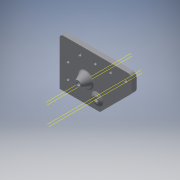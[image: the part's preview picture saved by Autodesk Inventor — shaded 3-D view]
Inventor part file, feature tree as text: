
AUTODESK INVENTOR PART (.ipt)
format: ipt  version: 2018 (Build 220112000, 112)  size: 218,112 bytes
history: native  units: in
note: dims shown in document units (in); Inventor stores cm internally (conversion verified against a paired STEP export)
features: sketch x8, extrude x6, plane x4, revolve x2, fillet x2, projected_geometry x2
ambient origin geometry x8: Origin, YZ Plane, XZ Plane, XY Plane, X Axis, Y Axis, Z Axis, Center Point
bodies: Solid1 (feature_tree)
feature tree (24):
  extrude  "Extrusion1"  Depth=0.7874in
  extrude  "Extrusion2"  Depth=3.5433in
  plane  "Work Plane2"
  revolve  "Revolution1"  [1 undecoded]
  extrude  "Extrusion3"  Depth=0.5512in
  extrude  "Extrusion4"  [1 undecoded]
  fillet  "Fillet1"  Radius=0.3543in
  extrude  "Extrusion5"  TaperAngle=90.0deg  [1 undecoded]
  plane  "Work Plane4"
  revolve  "Revolution2"  [1 undecoded]
  fillet  "Fillet2"  Radius=0.1654in
  extrude  "Extrusion6"  Depth=0.3937in
  sketch  "Sketch1"  dims[d0=0.7874in d1=0.7874in]
  sketch  "Sketch2"  dims[d2=3.5433in d3=3.5433in]
  plane  "Work Plane1"
  sketch  "Sketch3"  dims[d4=0.2362in d5=0.0in d6=0.1969in]
  sketch  "Sketch4"  dims[d7=1.2992in d8=0.5512in]
  projected_geometry  "Projected Loop1"
  sketch  "Sketch5"  dims[d9=0.2362in d10=0.0in d11=-0.0984in d12=0.3543in]
  sketch  "Sketch7"  dims[d13=0.3937in d14=90.0deg]
  plane  "Work Plane3"
  sketch  "Sketch8"  dims[d15=0.2362in d16=0.0in d17=0.1575in d18=0.1654in]
  projected_geometry  "Projected Loop2"
  sketch  "Sketch9"  dims[d19=0.315in d20=0.748in d21=0.748in d22=0.748in d23=0.315in d24=0.748in d25=0.748in d26=0.748in d27=0.2362in d28=0.0in d29=0.0787in d30=0.3543in d32=0.3543in d33=0.1969in d34=0.0in d35=0.0984in d36=0.1969in d37=0.0591in d38=0.0787in d39=90.0deg d40=0.1969in d42=0.3937in d43=0.0in d44=1.2598in]
note: 4 required parameter values undecoded (feature->parameter linkage not recoverable at this tier; creation-order binding heuristic only, values carry confidence <= 0.55)